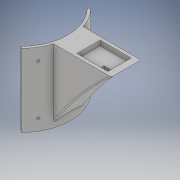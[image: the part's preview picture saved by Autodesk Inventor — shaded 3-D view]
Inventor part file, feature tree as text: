
AUTODESK INVENTOR PART (.ipt)
format: ipt  version: 2017 (Build 210142000, 142)  size: 206,848 bytes
history: native  units: in
note: dims shown in document units (in); Inventor stores cm internally (conversion verified against a paired STEP export)
features: sketch x5, extrude x4, plane x3, hole x2, shell x1, fillet x1
ambient origin geometry x8: Origin, YZ Plane, XZ Plane, XY Plane, X Axis, Y Axis, Z Axis, Center Point
bodies: Solid1 (feature_tree)
feature tree (16):
  extrude  "Extrusion1"  Depth=3.0in TaperAngle=0.0deg
  extrude  "Extrusion2"  Depth=2.0in TaperAngle=0.0deg
  extrude  "Extrusion5"  Depth=0.1in
  shell  "Shell2"  Thickness=2.3622in
  plane  "Work Plane2"
  extrude  "Extrusion6"  Depth=5.905in
  fillet  "Fillet3"  [1 undecoded]
  plane  "Work Plane3"
  hole  "Hole3"  [1 undecoded]
  plane  "Work Plane4"
  hole  "Hole4"  [1 undecoded]
  sketch  "Sketch1"  dims[d1=7.0in d2=3.0in d3=0.0in]
  sketch  "Sketch7"  dims[d8=0.5in d9=0.0in d43=2.0in d44=0.0in]
  sketch  "Sketch8"  dims[d45=0.1in d46=3.1496in d47=2.3622in]
  sketch  "Sketch9"  dims[d48=0.32in d49=5.905in d50=0.0in]
  sketch  "Sketch10"  dims[d51=10.0in d52=9.5in d53=7.375in d54=0.0in d55=0.125in d56=0.25in d57=0.25in d58=0.25in d59=0.75in d60=0.375in d61=0.25in d62=0.5635in d63=1.0in d64=0.8108in d65=0.25in d66=0.25in d67=0.25in d68=0.75in d69=0.375in d70=0.25in d71=0.5635in d72=1.0in d73=0.8108in]
note: 3 required parameter values undecoded (feature->parameter linkage not recoverable at this tier; creation-order binding heuristic only, values carry confidence <= 0.55)
